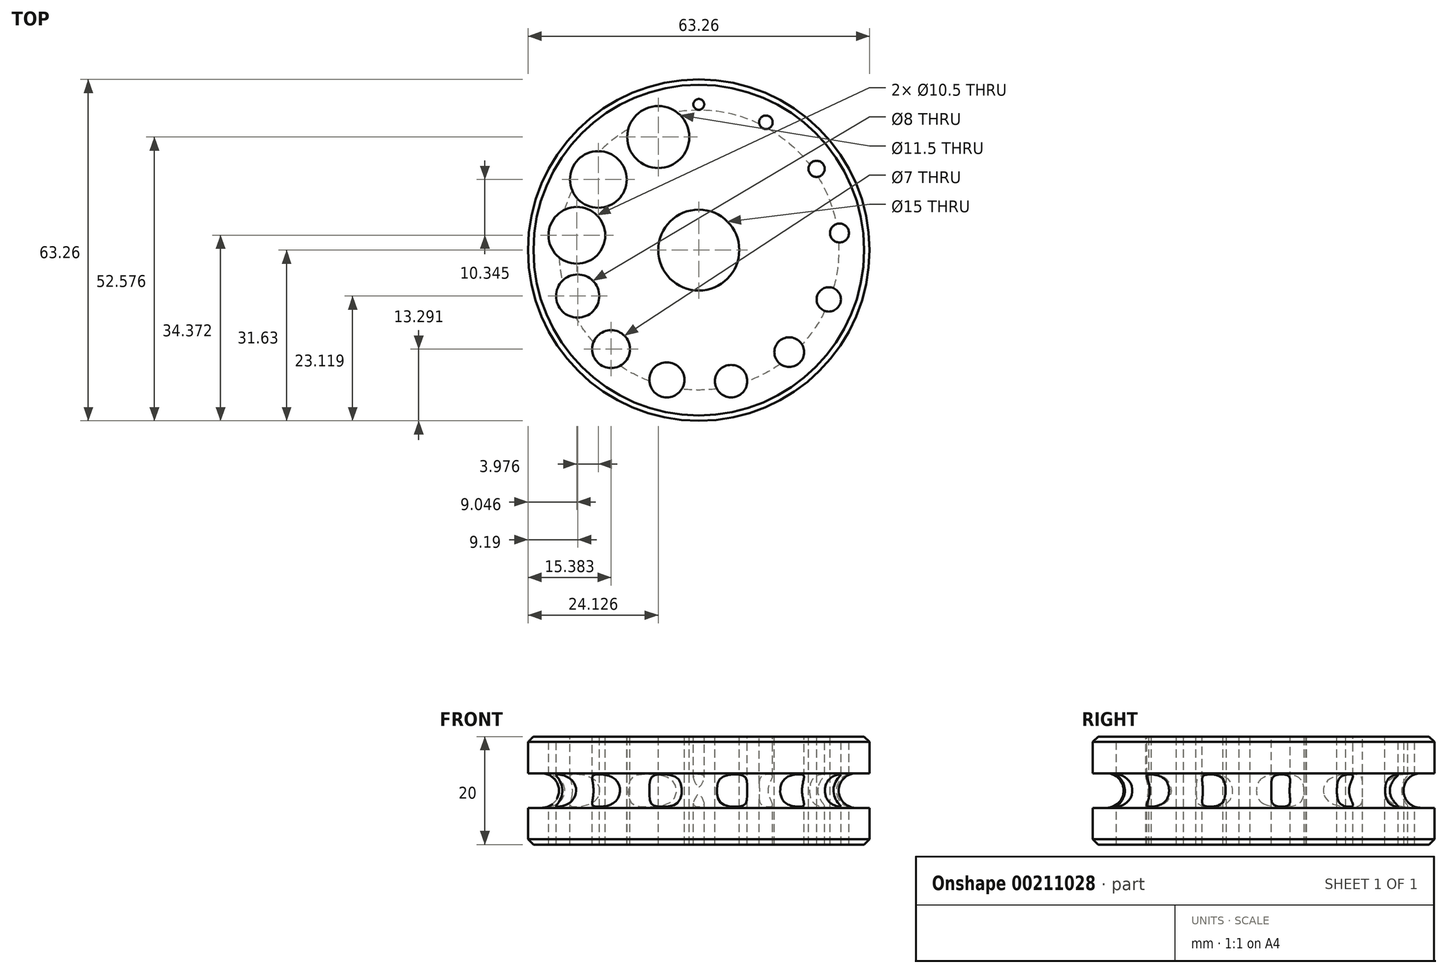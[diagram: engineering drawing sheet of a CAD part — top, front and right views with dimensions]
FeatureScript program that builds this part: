
annotation { "Feature Type Name" : "Feature", "Feature Type Description" : "" }
export const myFeature = defineFeature(function(context is Context, id is Id, definition is map)
    precondition{}
    {
        {
            var Q0;
            Q0=qCreatedBy(makeId("Front.planeOp"),FACE);
            var sketch = newSketch(context, id + "F0", { "sketchPlane" : qUnion([Q0])});
            skLineSegment(sketch, "E0.bottom", {"start": v(0, 0) * mm, "end": v(31.62, 0) * mm});
            skLineSegment(sketch, "E0.top", {"start": v(0, 20) * mm, "end": v(31.62, 20) * mm});
            skLineSegment(sketch, "E0.left", {"start": v(0, 0) * mm, "end": v(0, 20) * mm});
            skLineSegment(sketch, "E1", {"start": v(31.62, 20) * mm, "end": v(31.62, 13.2) * mm});
            skArc(sketch, "E2", {"start": v(29.12, 13.2) * mm, "mid": v(25.92, 10) * mm, "end": v(29.12, 6.8) * mm});
            skLineSegment(sketch, "E3", {"start": v(29.12, 13.2) * mm, "end": v(31.62, 13.2) * mm});
            skLineSegment(sketch, "E4", {"start": v(29.12, 6.8) * mm, "end": v(31.62, 6.8) * mm});
            skLineSegment(sketch, "E5.trimOffspring", {"start": v(31.62, 6.8) * mm, "end": v(31.62, 0) * mm});
            skSolve(sketch);
        }
        {
            var Q0;
            Q0 = qSketchRegion(id + "F0", true);
            var Q1;
            Q1=sQuery(id+"F0.wireOp",EDGE,"E0.left");
            revolve(context, id + "F1", {"entities" : qUnion([Q0]), "axis" : qUnion([Q1]), "revolveType" : RevolveType.FULL});
        }
        {
            var Q0;
            Q0=makeQuery(id+"F1.opRevolve","SWEPT_FACE",FACE,{"disambiguationData":[OSD([sQuery(id+"F0.wireOp",EDGE,"E0.top")])]});
            var sketch = newSketch(context, id + "F2", { "sketchPlane" : qUnion([Q0])});
            skCircle(sketch, "E6", {"center": v(0, 0) * mm, "radius": 28 * mm, "construction": true});
            skLineSegment(sketch, "E7", {"start": v(0, 31.62) * mm, "end": v(0, 0) * mm, "construction": true});
            skCircle(sketch, "E8", {"center": v(0, 27) * mm, "radius": 1 * mm});
            skLineSegment(sketch, "E9.1.0", {"start": v(-14.7, 28) * mm, "end": v(0, 0) * mm, "construction": true});
            skLineSegment(sketch, "E9.2.0", {"start": v(-26.03, 17.97) * mm, "end": v(0, 0) * mm, "construction": true});
            skLineSegment(sketch, "E9.3.0", {"start": v(-31.4, 3.81) * mm, "end": v(0, 0) * mm, "construction": true});
            skLineSegment(sketch, "E9.4.0", {"start": v(-29.57, -11.21) * mm, "end": v(0, 0) * mm, "construction": true});
            skLineSegment(sketch, "E9.5.0", {"start": v(-20.97, -23.67) * mm, "end": v(0, 0) * mm, "construction": true});
            skLineSegment(sketch, "E9.6.0", {"start": v(-7.57, -30.7) * mm, "end": v(0, 0) * mm, "construction": true});
            skLineSegment(sketch, "E9.7.0", {"start": v(7.57, -30.7) * mm, "end": v(0, 0) * mm, "construction": true});
            skLineSegment(sketch, "E9.8.0", {"start": v(20.97, -23.67) * mm, "end": v(0, 0) * mm, "construction": true});
            skLineSegment(sketch, "E9.9.0", {"start": v(29.57, -11.21) * mm, "end": v(0, 0) * mm, "construction": true});
            skLineSegment(sketch, "E9.10.0", {"start": v(31.4, 3.81) * mm, "end": v(0, 0) * mm, "construction": true});
            skLineSegment(sketch, "E9.11.0", {"start": v(26.03, 17.97) * mm, "end": v(0, 0) * mm, "construction": true});
            skLineSegment(sketch, "E9.12.0", {"start": v(14.7, 28) * mm, "end": v(0, 0) * mm, "construction": true});
            skCircle(sketch, "E10", {"center": v(12.43, 23.69) * mm, "radius": 1.25 * mm});
            skCircle(sketch, "E11", {"center": v(21.8, 15.05) * mm, "radius": 1.5 * mm});
            skCircle(sketch, "E12", {"center": v(26.06, 3.16) * mm, "radius": 1.75 * mm});
            skCircle(sketch, "E13", {"center": v(24.08, -9.13) * mm, "radius": 2.25 * mm});
            skCircle(sketch, "E14", {"center": v(16.74, -18.9) * mm, "radius": 2.75 * mm});
            skCircle(sketch, "E15", {"center": v(5.98, -24.27) * mm, "radius": 3 * mm});
            skCircle(sketch, "E16", {"center": v(-5.92, -24.03) * mm, "radius": 3.25 * mm});
            skCircle(sketch, "E17", {"center": v(-16.25, -18.34) * mm, "radius": 3.5 * mm});
            skCircle(sketch, "E18", {"center": v(-22.44, -8.51) * mm, "radius": 4 * mm});
            skCircle(sketch, "E19", {"center": v(-22.58, 2.74) * mm, "radius": 5.25 * mm});
            skCircle(sketch, "E20", {"center": v(0, 0) * mm, "radius": 7.5 * mm});
            skLineSegment(sketch, "E21", {"start": v(0, 0) * mm, "end": v(-10.67, 29.77) * mm, "construction": true});
            skLineSegment(sketch, "E22", {"start": v(0, 0) * mm, "end": v(-25.87, 18.2) * mm, "construction": true});
            skCircle(sketch, "E23", {"center": v(-18.6, 13.09) * mm, "radius": 5.25 * mm});
            skCircle(sketch, "E24", {"center": v(-7.5, 20.95) * mm, "radius": 5.75 * mm});
            skSolve(sketch);
        }
        {
            var Q0;
            Q0 = qSketchRegion(id + "F2", true);
            extrude(context, id + "F3", {"entities" : qUnion([Q0]), "operationType" : NewBodyOperationType.REMOVE, "oppositeDirection" : true, "depth" : 25 * mm});
        }
        {
            var Q0;
            Q0=makeQuery(id+"F1.opRevolve","SWEPT_EDGE",EDGE,{"disambiguationData":[OSD([sQuery(id+"F0.wireOp",EDGE,"E0.top"),sQuery(id+"F0.wireOp",EDGE,"c85ffed4-4e02-4304-a71e-ca71a9594cdb.trimOffspring")])]});
            var Q1;
            Q1=makeQuery(id+"F1.opRevolve","SWEPT_EDGE",EDGE,{"disambiguationData":[OSD([sQuery(id+"F0.wireOp",EDGE,"E0.bottom"),sQuery(id+"F0.wireOp",EDGE,"E0.right")])]});
            chamfer(context, id + "F4", {"entities" : qUnion([Q0, Q1]), "width" : 1 * mm, "tangentPropagation" : true});
        }
        {
            var Q0;
            Q0 = qSketchRegion(id + "F2", true);
            extrude(context, id + "F5", {"entities" : qUnion([Q0]), "operationType" : NewBodyOperationType.REMOVE, "endBound" : BoundingType.THROUGH_ALL, "oppositeDirection" : true, "depth" : 25 * mm});
        }
    });
